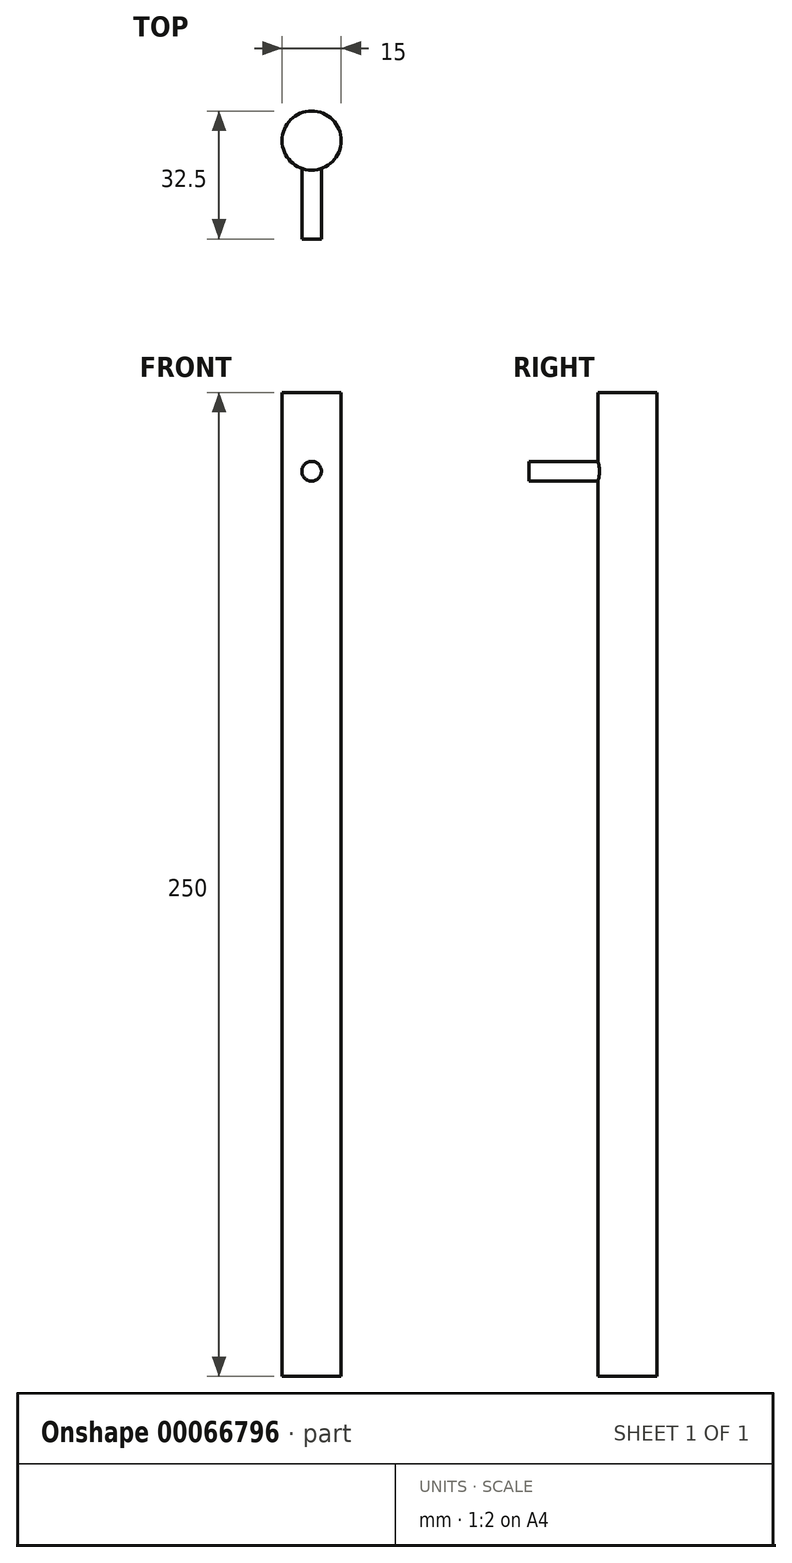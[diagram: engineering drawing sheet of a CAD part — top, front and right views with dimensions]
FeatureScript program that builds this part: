
annotation { "Feature Type Name" : "Feature", "Feature Type Description" : "" }
export const myFeature = defineFeature(function(context is Context, id is Id, definition is map)
    precondition{}
    {
        {
            var Q0;
            Q0=qCreatedBy(makeId("Top.planeOp"),FACE);
            var sketch = newSketch(context, id + "F0", { "sketchPlane" : qUnion([Q0])});
            skCircle(sketch, "E0", {"center": v(0, 0) * mm, "radius": 7.5 * mm});
            skSolve(sketch);
        }
        {
            var Q0;
            Q0=makeQuery(id+"F0.imprint","IMPRINT",FACE,{"disambiguationData":[TD([[makeQuery(id+"F0.imprint","IMPRINT",EDGE,{"derivedFrom":sQuery(id+"F0.wireOp",EDGE,"E0")}),1.0]])]});
            extrude(context, id + "F1", {"entities" : qUnion([Q0]), "depth" : 250 * mm});
        }
        {
            var Q0;
            Q0=qCreatedBy(makeId("Front.planeOp"),FACE);
            var sketch = newSketch(context, id + "F2", { "sketchPlane" : qUnion([Q0])});
            skCircle(sketch, "E1", {"center": v(0, 230) * mm, "radius": 2.5 * mm});
            skSolve(sketch);
        }
        {
            var Q0;
            Q0 = qSketchRegion(id + "F2", true);
            extrude(context, id + "F3", {"entities" : qUnion([Q0]), "operationType" : NewBodyOperationType.ADD, "depth" : 25 * mm});
        }
    });
